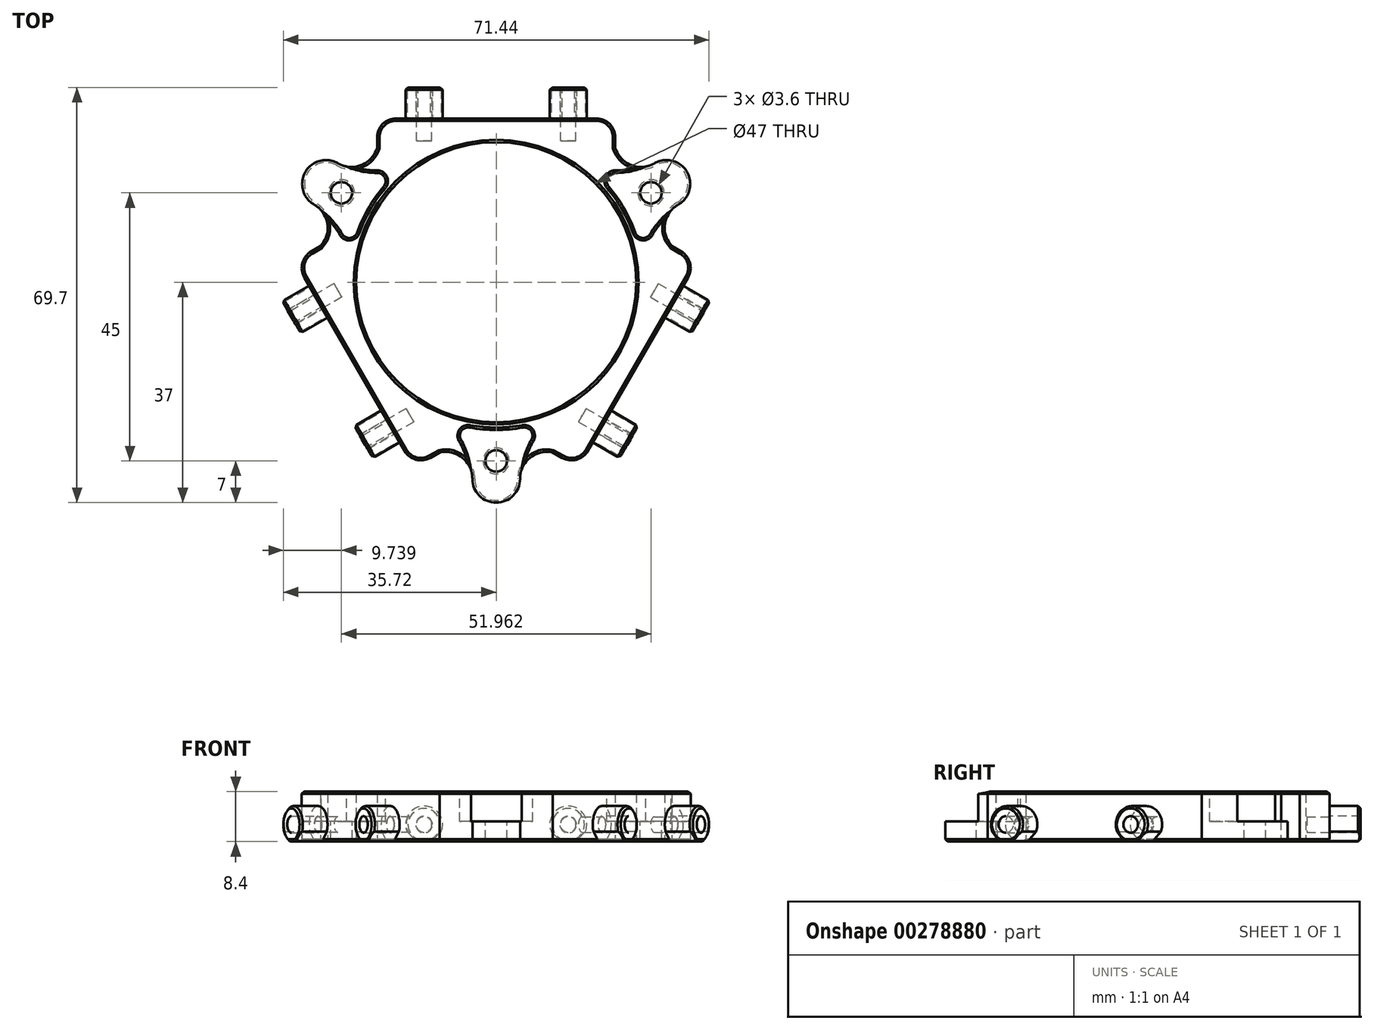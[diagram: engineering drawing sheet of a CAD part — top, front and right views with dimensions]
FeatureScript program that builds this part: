
annotation { "Feature Type Name" : "Feature", "Feature Type Description" : "" }
export const myFeature = defineFeature(function(context is Context, id is Id, definition is map)
    precondition{}
    {
        {
            var Q0;
            Q0=qCreatedBy(makeId("Top.planeOp"),FACE);
            var sketch = newSketch(context, id + "F0", { "sketchPlane" : qUnion([Q0])});
            skLineSegment(sketch, "E0", {"start": v(0, 27.5) * mm, "end": v(12, 27.5) * mm});
            skLineSegment(sketch, "E1", {"start": v(12, 27.5) * mm, "end": v(20, 27.5) * mm});
            skLineSegment(sketch, "E2", {"start": v(20, 27.5) * mm, "end": v(20, 22.5) * mm});
            skLineSegment(sketch, "E3.MirrorCS", {"start": v(0, 27.5) * mm, "end": v(-12, 27.5) * mm});
            skLineSegment(sketch, "E4.MirrorCS", {"start": v(-12, 27.5) * mm, "end": v(-20, 27.5) * mm});
            skLineSegment(sketch, "E5.MirrorCS", {"start": v(-20, 27.5) * mm, "end": v(-20, 22.5) * mm});
            skLineSegment(sketch, "E6.1.0", {"start": v(-13.82, -31.07) * mm, "end": v(-9.49, -28.57) * mm});
            skLineSegment(sketch, "E6.1.1", {"start": v(-33.82, 3.57) * mm, "end": v(-29.49, 6.07) * mm});
            skLineSegment(sketch, "E6.1.2", {"start": v(-23.82, -13.75) * mm, "end": v(-29.82, -3.36) * mm});
            skLineSegment(sketch, "E6.1.3", {"start": v(-29.82, -3.36) * mm, "end": v(-33.82, 3.57) * mm});
            skLineSegment(sketch, "E6.1.4", {"start": v(-23.82, -13.75) * mm, "end": v(-17.82, -24.14) * mm});
            skLineSegment(sketch, "E6.1.5", {"start": v(-17.82, -24.14) * mm, "end": v(-13.82, -31.07) * mm});
            skLineSegment(sketch, "E6.2.0", {"start": v(33.82, 3.57) * mm, "end": v(29.49, 6.07) * mm});
            skLineSegment(sketch, "E6.2.1", {"start": v(13.82, -31.07) * mm, "end": v(9.49, -28.57) * mm});
            skLineSegment(sketch, "E6.2.2", {"start": v(23.82, -13.75) * mm, "end": v(17.82, -24.14) * mm});
            skLineSegment(sketch, "E6.2.3", {"start": v(17.82, -24.14) * mm, "end": v(13.82, -31.07) * mm});
            skLineSegment(sketch, "E6.2.4", {"start": v(23.82, -13.75) * mm, "end": v(29.82, -3.36) * mm});
            skLineSegment(sketch, "E6.2.5", {"start": v(29.82, -3.36) * mm, "end": v(33.82, 3.57) * mm});
            skPoint(sketch, "E6.center", {"position": v(0, 0) * mm});
            skArc(sketch, "E7", {"start": v(-8.76, -23.41) * mm, "mid": v(0, -25) * mm, "end": v(8.76, -23.41) * mm});
            skCircle(sketch, "E8", {"center": v(0, -33) * mm, "radius": 4 * mm});
            skArc(sketch, "E9", {"start": v(8.76, -23.41) * mm, "mid": v(5.25, -27.65) * mm, "end": v(4, -33) * mm});
            skArc(sketch, "E10.MirrorCS", {"start": v(-8.76, -23.41) * mm, "mid": v(-5.25, -27.65) * mm, "end": v(-4, -33) * mm});
            skCircle(sketch, "E11", {"center": v(0, 0) * mm, "radius": 23.5 * mm});
            skArc(sketch, "E12", {"start": v(9.49, -28.57) * mm, "mid": v(5.67, -29.46) * mm, "end": v(4, -33) * mm});
            skArc(sketch, "E13.MirrorCS", {"start": v(-9.49, -28.57) * mm, "mid": v(-5.67, -29.46) * mm, "end": v(-4, -33) * mm});
            skCircle(sketch, "E14.1.0", {"center": v(28.58, 16.5) * mm, "radius": 4 * mm});
            skArc(sketch, "E14.1.1", {"start": v(20, 22.5) * mm, "mid": v(22.68, 19.64) * mm, "end": v(26.58, 19.96) * mm});
            skArc(sketch, "E14.1.2", {"start": v(29.49, 6.07) * mm, "mid": v(28.35, 9.82) * mm, "end": v(30.58, 13.04) * mm});
            skCircle(sketch, "E14.2.0", {"center": v(-28.58, 16.5) * mm, "radius": 4 * mm});
            skArc(sketch, "E14.2.1", {"start": v(-29.49, 6.07) * mm, "mid": v(-28.35, 9.82) * mm, "end": v(-30.58, 13.04) * mm});
            skArc(sketch, "E14.2.2", {"start": v(-20, 22.5) * mm, "mid": v(-22.68, 19.64) * mm, "end": v(-26.58, 19.96) * mm});
            skSolve(sketch);
        }
        {
            var Q0;
            Q0=qSketchRegion(id+"F0",true);
            extrude(context, id + "F1", {"entities" : qUnion([Q0]), "depth" : 8.4 * mm, "offsetDistance" : 25 * mm});
        }
        {
            var Q0;
            Q0=makeQuery(id+"F1.opExtrude","SWEPT_FACE",FACE,{"disambiguationData":[OSD([sQuery(id+"F0.wireOp",EDGE,"E0"),sQuery(id+"F0.wireOp",EDGE,"E1"),sQuery(id+"F0.wireOp",EDGE,"E3.MirrorCS"),sQuery(id+"F0.wireOp",EDGE,"E4.MirrorCS")])]});
            var sketch = newSketch(context, id + "F2", { "sketchPlane" : qUnion([Q0])});
            skCircle(sketch, "E15.cCircle", {"center": v(-12.1, 2.86) * mm, "radius": 2.86 * mm, "construction": true});
            skLineSegment(sketch, "E15.0", {"start": v(-13.29, 5.73) * mm, "end": v(-10.91, 5.73) * mm});
            skLineSegment(sketch, "E15.1", {"start": v(-10.91, 5.73) * mm, "end": v(-9.24, 4.05) * mm});
            skLineSegment(sketch, "E15.2", {"start": v(-9.24, 4.05) * mm, "end": v(-9.24, 1.68) * mm});
            skLineSegment(sketch, "E15.3", {"start": v(-9.24, 1.68) * mm, "end": v(-10.91, 0) * mm});
            skLineSegment(sketch, "E15.4", {"start": v(-10.91, 0) * mm, "end": v(-13.29, 0) * mm});
            skLineSegment(sketch, "E15.5", {"start": v(-13.29, 0) * mm, "end": v(-14.96, 1.68) * mm});
            skLineSegment(sketch, "E15.6", {"start": v(-14.96, 1.68) * mm, "end": v(-14.96, 4.05) * mm});
            skLineSegment(sketch, "E15.7", {"start": v(-14.96, 4.05) * mm, "end": v(-13.29, 5.73) * mm});
            skPoint(sketch, "E15.0.midPoint", {"position": v(-12.1, 5.73) * mm});
            skArc(sketch, "E16", {"start": v(-9.24, 1.68) * mm, "mid": v(-12.1, 5.96) * mm, "end": v(-14.96, 1.68) * mm});
            skLineSegment(sketch, "E17.MirrorCS", {"start": v(10.91, 5.73) * mm, "end": v(9.24, 4.05) * mm});
            skLineSegment(sketch, "E18.MirrorCS", {"start": v(9.24, 4.05) * mm, "end": v(9.24, 1.68) * mm});
            skLineSegment(sketch, "E19.MirrorCS", {"start": v(14.96, 1.68) * mm, "end": v(14.96, 4.05) * mm});
            skLineSegment(sketch, "E20.MirrorCS", {"start": v(9.24, 1.68) * mm, "end": v(10.91, 0) * mm});
            skLineSegment(sketch, "E21.MirrorCS", {"start": v(14.96, 4.05) * mm, "end": v(13.29, 5.73) * mm});
            skLineSegment(sketch, "E22.MirrorCS", {"start": v(13.29, 5.73) * mm, "end": v(10.91, 5.73) * mm});
            skLineSegment(sketch, "E23.MirrorCS", {"start": v(10.91, 0) * mm, "end": v(13.29, 0) * mm});
            skLineSegment(sketch, "E24.MirrorCS", {"start": v(13.29, 0) * mm, "end": v(14.96, 1.68) * mm});
            skArc(sketch, "E25.MirrorCS", {"start": v(9.24, 1.68) * mm, "mid": v(12.1, 5.96) * mm, "end": v(14.96, 1.68) * mm});
            skPoint(sketch, "E26.MirrorP", {"position": v(12.1, 5.73) * mm});
            skCircle(sketch, "E27.MirrorC", {"center": v(12.1, 2.86) * mm, "radius": 2.86 * mm, "construction": true});
            skCircle(sketch, "E28", {"center": v(-12.1, 2.86) * mm, "radius": 1.4 * mm});
            skCircle(sketch, "E29.MirrorC", {"center": v(12.1, 2.86) * mm, "radius": 1.4 * mm});
            skSolve(sketch);
        }
        {
            var Q0;
            Q0=qSketchRegion(id+"F2",true);
            extrude(context, id + "F3", {"entities" : qUnion([Q0]), "depth" : 5.2 * mm, "offsetDistance" : 25 * mm});
        }
        {
            var Q0;
            Q0=makeQuery(id+"F3.opExtrude","SWEPT_BODY",BODY,{"disambiguationData":[OSD([sQuery(id+"F2.wireOp",EDGE,"E15.0"),sQuery(id+"F2.wireOp",EDGE,"E15.1"),sQuery(id+"F2.wireOp",EDGE,"E15.2"),sQuery(id+"F2.wireOp",EDGE,"E15.3"),sQuery(id+"F2.wireOp",EDGE,"E15.4"),sQuery(id+"F2.wireOp",EDGE,"E15.5"),sQuery(id+"F2.wireOp",EDGE,"E15.6"),sQuery(id+"F2.wireOp",EDGE,"E15.7")])]});
            var Q1;
            Q1=makeQuery(id+"F3.opExtrude","SWEPT_BODY",BODY,{"disambiguationData":[OSD([sQuery(id+"F2.wireOp",EDGE,"E20.MirrorCS"),sQuery(id+"F2.wireOp",EDGE,"E23.MirrorCS"),sQuery(id+"F2.wireOp",EDGE,"E24.MirrorCS"),sQuery(id+"F2.wireOp",EDGE,"E25.MirrorCS")])]});
            var Q2;
            Q2=makeQuery(id+"F1.opExtrude","CAP_EDGE",EDGE,{"disambiguationData":[OSD([sQuery(id+"F0.wireOp",EDGE,"E11")])],"isStart":false});
            circularPattern(context, id + "F4", {"operationType" : NewBodyOperationType.ADD, "entities" : qUnion([Q0, Q1]), "axis" : qUnion([Q2]), "angle" : 360 * degree, "instanceCount" : 3, "equalSpace" : true});
        }
        {
            var Q0;
            Q0=makeQuery(id+"F3.opExtrude","CAP_FACE",FACE,{"disambiguationData":[OSD([sQuery(id+"F2.wireOp",EDGE,"E15.3"),sQuery(id+"F2.wireOp",EDGE,"E15.4"),sQuery(id+"F2.wireOp",EDGE,"E15.5"),sQuery(id+"F2.wireOp",EDGE,"E16")])],"isStart":false});
            var sketch = newSketch(context, id + "F5", { "sketchPlane" : qUnion([Q0])});
            skCircle(sketch, "E30", {"center": v(-12.1, 2.86) * mm, "radius": 1.3 * mm});
            skCircle(sketch, "E31.MirrorC", {"center": v(12.1, 2.86) * mm, "radius": 1.3 * mm});
            skSolve(sketch);
        }
        {
            var Q0;
            Q0=qSketchRegion(id+"F5",true);
            extrude(context, id + "F6", {"entities" : qUnion([Q0]), "oppositeDirection" : true, "depth" : 9 * mm, "offsetDistance" : 25 * mm});
        }
        {
            var Q0;
            Q0=makeQuery(id+"F6.opExtrude","SWEPT_BODY",BODY,{"disambiguationData":[OSD([sQuery(id+"F5.wireOp",EDGE,"E31.MirrorC")])]});
            var Q1;
            Q1=makeQuery(id+"F6.opExtrude","SWEPT_BODY",BODY,{"disambiguationData":[OSD([sQuery(id+"F5.wireOp",EDGE,"E30")])]});
            var Q2;
            Q2=makeQuery(id+"F1.opExtrude","CAP_EDGE",EDGE,{"disambiguationData":[OSD([sQuery(id+"F0.wireOp",EDGE,"E11")])],"isStart":false});
            circularPattern(context, id + "F7", {"operationType" : NewBodyOperationType.REMOVE, "entities" : qUnion([Q0, Q1]), "axis" : qUnion([Q2]), "angle" : 360 * degree, "instanceCount" : 3, "equalSpace" : true});
        }
        {
            var Q0;
            Q0=makeQuery(id+"F1.opExtrude","CAP_FACE",FACE,{"disambiguationData":[OSD([sQuery(id+"F0.wireOp",EDGE,"4484d7a0-2c50-4ab7-845c-1fad09a73396"),sQuery(id+"F0.wireOp",EDGE,"vunMmcyM-OmEz-jSXp-RP42-2TM2nteFIjq3"),sQuery(id+"F0.wireOp",EDGE,"kAdxAM4n-0fVD-Q49A-3DVH-t19awp9mxCRN"),sQuery(id+"F0.wireOp",EDGE,"1fc718da-6f13-47b3-b5a0-f714b977743f0.MirrorCS"),sQuery(id+"F0.wireOp",EDGE,"0c3f0dc6-742d-4421-8c8e-992fc040e4260.MirrorCS"),sQuery(id+"F0.wireOp",EDGE,"NR2aZ9zS-O8kZ-dOxt-Ha0G-w07LVY2dGel9"),sQuery(id+"F0.wireOp",EDGE,"E0"),sQuery(id+"F0.wireOp",EDGE,"E1"),sQuery(id+"F0.wireOp",EDGE,"E2"),sQuery(id+"F0.wireOp",EDGE,"E3.MirrorCS"),sQuery(id+"F0.wireOp",EDGE,"E4.MirrorCS"),sQuery(id+"F0.wireOp",EDGE,"E5.MirrorCS"),sQuery(id+"F0.wireOp",EDGE,"b799197c-b9e2-4d90-802a-dec7aafa3731.1.0"),sQuery(id+"F0.wireOp",EDGE,"b799197c-b9e2-4d90-802a-dec7aafa3731.1.1"),sQuery(id+"F0.wireOp",EDGE,"b799197c-b9e2-4d90-802a-dec7aafa3731.1.2"),sQuery(id+"F0.wireOp",EDGE,"b799197c-b9e2-4d90-802a-dec7aafa3731.1.3"),sQuery(id+"F0.wireOp",EDGE,"b799197c-b9e2-4d90-802a-dec7aafa3731.1.4"),sQuery(id+"F0.wireOp",EDGE,"b799197c-b9e2-4d90-802a-dec7aafa3731.1.5"),sQuery(id+"F0.wireOp",EDGE,"b799197c-b9e2-4d90-802a-dec7aafa3731.2.0"),sQuery(id+"F0.wireOp",EDGE,"b799197c-b9e2-4d90-802a-dec7aafa3731.2.1"),sQuery(id+"F0.wireOp",EDGE,"b799197c-b9e2-4d90-802a-dec7aafa3731.2.2"),sQuery(id+"F0.wireOp",EDGE,"b799197c-b9e2-4d90-802a-dec7aafa3731.2.3"),sQuery(id+"F0.wireOp",EDGE,"b799197c-b9e2-4d90-802a-dec7aafa3731.2.4"),sQuery(id+"F0.wireOp",EDGE,"b799197c-b9e2-4d90-802a-dec7aafa3731.2.5"),sQuery(id+"F0.wireOp",EDGE,"Wg4TRRuH-37hh-Xavb-2tcF-YoE0x18wPgdB"),sQuery(id+"F0.wireOp",EDGE,"0f9c7b85-d36a-485b-916f-4e3243d4aea60.MirrorCS"),sQuery(id+"F0.wireOp",EDGE,"b2d11125-5d0d-4662-a4de-013f4188032f.1.0"),sQuery(id+"F0.wireOp",EDGE,"b2d11125-5d0d-4662-a4de-013f4188032f.1.2"),sQuery(id+"F0.wireOp",EDGE,"b2d11125-5d0d-4662-a4de-013f4188032f.1.3"),sQuery(id+"F0.wireOp",EDGE,"b2d11125-5d0d-4662-a4de-013f4188032f.1.7"),sQuery(id+"F0.wireOp",EDGE,"b2d11125-5d0d-4662-a4de-013f4188032f.1.8"),sQuery(id+"F0.wireOp",EDGE,"b2d11125-5d0d-4662-a4de-013f4188032f.1.9"),sQuery(id+"F0.wireOp",EDGE,"b2d11125-5d0d-4662-a4de-013f4188032f.1.10"),sQuery(id+"F0.wireOp",EDGE,"b2d11125-5d0d-4662-a4de-013f4188032f.2.0"),sQuery(id+"F0.wireOp",EDGE,"b2d11125-5d0d-4662-a4de-013f4188032f.2.2"),sQuery(id+"F0.wireOp",EDGE,"b2d11125-5d0d-4662-a4de-013f4188032f.2.3"),sQuery(id+"F0.wireOp",EDGE,"b2d11125-5d0d-4662-a4de-013f4188032f.2.7"),sQuery(id+"F0.wireOp",EDGE,"b2d11125-5d0d-4662-a4de-013f4188032f.2.8"),sQuery(id+"F0.wireOp",EDGE,"b2d11125-5d0d-4662-a4de-013f4188032f.2.9"),sQuery(id+"F0.wireOp",EDGE,"b2d11125-5d0d-4662-a4de-013f4188032f.2.10")])],"isStart":false});
            var sketch = newSketch(context, id + "F8", { "sketchPlane" : qUnion([Q0])});
            skArc(sketch, "E32", {"start": v(-8.86, -23.16) * mm, "mid": v(0, -24.8) * mm, "end": v(8.86, -23.16) * mm});
            skCircle(sketch, "E33", {"center": v(0, -33) * mm, "radius": 4.2 * mm});
            skArc(sketch, "E34", {"start": v(8.86, -23.16) * mm, "mid": v(5.35, -27.52) * mm, "end": v(4.2, -33) * mm});
            skArc(sketch, "E35.MirrorCS", {"start": v(-8.86, -23.16) * mm, "mid": v(-5.35, -27.52) * mm, "end": v(-4.2, -33) * mm});
            skArc(sketch, "E36.1.0", {"start": v(24.5, 3.9) * mm, "mid": v(26.51, 9.13) * mm, "end": v(30.68, 12.86) * mm});
            skArc(sketch, "E36.1.1", {"start": v(24.5, 3.9) * mm, "mid": v(21.48, 12.4) * mm, "end": v(15.63, 19.26) * mm});
            skArc(sketch, "E36.1.2", {"start": v(15.63, 19.26) * mm, "mid": v(21.16, 18.4) * mm, "end": v(26.48, 20.14) * mm});
            skCircle(sketch, "E36.1.3", {"center": v(28.58, 16.5) * mm, "radius": 4.2 * mm});
            skArc(sketch, "E36.2.0", {"start": v(-15.63, 19.26) * mm, "mid": v(-21.16, 18.4) * mm, "end": v(-26.48, 20.14) * mm});
            skArc(sketch, "E36.2.1", {"start": v(-15.63, 19.26) * mm, "mid": v(-21.48, 12.4) * mm, "end": v(-24.5, 3.9) * mm});
            skArc(sketch, "E36.2.2", {"start": v(-24.5, 3.9) * mm, "mid": v(-26.51, 9.13) * mm, "end": v(-30.68, 12.86) * mm});
            skCircle(sketch, "E36.2.3", {"center": v(-28.58, 16.5) * mm, "radius": 4.2 * mm});
            skSolve(sketch);
        }
        {
            var Q0;
            Q0=qSketchRegion(id+"F8",true);
            extrude(context, id + "F9", {"entities" : qUnion([Q0]), "oppositeDirection" : true, "depth" : 5 * mm, "offsetDistance" : 25 * mm});
        }
        {
            var Q0;
            Q0=makeQuery(id+"F9.opExtrude","SWEPT_EDGE",EDGE,{"disambiguationData":[OSD([sQuery(id+"F8.wireOp",EDGE,"E32"),sQuery(id+"F8.wireOp",EDGE,"E34")])]});
            var Q1;
            Q1=makeQuery(id+"F9.opExtrude","SWEPT_EDGE",EDGE,{"disambiguationData":[OSD([sQuery(id+"F8.wireOp",EDGE,"E32"),sQuery(id+"F8.wireOp",EDGE,"E35.MirrorCS")])]});
            var Q2;
            Q2=makeQuery(id+"F9.opExtrude","SWEPT_EDGE",EDGE,{"disambiguationData":[OSD([sQuery(id+"F8.wireOp",EDGE,"E36.1.0"),sQuery(id+"F8.wireOp",EDGE,"E36.1.1")])]});
            var Q3;
            Q3=makeQuery(id+"F9.opExtrude","SWEPT_EDGE",EDGE,{"disambiguationData":[OSD([sQuery(id+"F8.wireOp",EDGE,"E36.1.1"),sQuery(id+"F8.wireOp",EDGE,"E36.1.2")])]});
            var Q4;
            Q4=makeQuery(id+"F9.opExtrude","SWEPT_EDGE",EDGE,{"disambiguationData":[OSD([sQuery(id+"F8.wireOp",EDGE,"E36.2.0"),sQuery(id+"F8.wireOp",EDGE,"E36.2.1")])]});
            var Q5;
            Q5=makeQuery(id+"F9.opExtrude","SWEPT_EDGE",EDGE,{"disambiguationData":[OSD([sQuery(id+"F8.wireOp",EDGE,"E36.2.1"),sQuery(id+"F8.wireOp",EDGE,"E36.2.2")])]});
            fillet(context, id + "F10", {"entities" : qUnion([Q0, Q1, Q2, Q3, Q4, Q5]), "radius" : 1.4 * mm, "tangentPropagation" : true, "allowEdgeOverflow" : false});
        }
        {
            var Q0;
            Q0=makeQuery(id+"F9.opExtrude","SWEPT_BODY",BODY,{"disambiguationData":[OSD([sQuery(id+"F8.wireOp",EDGE,"E32"),sQuery(id+"F8.wireOp",EDGE,"E33"),sQuery(id+"F8.wireOp",EDGE,"E34"),sQuery(id+"F8.wireOp",EDGE,"E35.MirrorCS")])]});
            var Q1;
            Q1=makeQuery(id+"F9.opExtrude","SWEPT_BODY",BODY,{"disambiguationData":[OSD([sQuery(id+"F8.wireOp",EDGE,"E36.1.0"),sQuery(id+"F8.wireOp",EDGE,"E36.1.1"),sQuery(id+"F8.wireOp",EDGE,"E36.1.2"),sQuery(id+"F8.wireOp",EDGE,"E36.1.3")])]});
            var Q2;
            Q2=makeQuery(id+"F9.opExtrude","SWEPT_BODY",BODY,{"disambiguationData":[OSD([sQuery(id+"F8.wireOp",EDGE,"E36.2.0"),sQuery(id+"F8.wireOp",EDGE,"E36.2.1"),sQuery(id+"F8.wireOp",EDGE,"E36.2.2"),sQuery(id+"F8.wireOp",EDGE,"E36.2.3")])]});
            var Q3;
            Q3=makeQuery(id+"F1.opExtrude","SWEPT_BODY",BODY,{"disambiguationData":[OSD([sQuery(id+"F0.wireOp",EDGE,"E0"),sQuery(id+"F0.wireOp",EDGE,"E1"),sQuery(id+"F0.wireOp",EDGE,"E2"),sQuery(id+"F0.wireOp",EDGE,"E3.MirrorCS"),sQuery(id+"F0.wireOp",EDGE,"E4.MirrorCS"),sQuery(id+"F0.wireOp",EDGE,"E5.MirrorCS"),sQuery(id+"F0.wireOp",EDGE,"E6.1.0"),sQuery(id+"F0.wireOp",EDGE,"E6.1.1"),sQuery(id+"F0.wireOp",EDGE,"E6.1.2"),sQuery(id+"F0.wireOp",EDGE,"E6.1.3"),sQuery(id+"F0.wireOp",EDGE,"E6.1.4"),sQuery(id+"F0.wireOp",EDGE,"E6.1.5"),sQuery(id+"F0.wireOp",EDGE,"E6.2.0"),sQuery(id+"F0.wireOp",EDGE,"E6.2.1"),sQuery(id+"F0.wireOp",EDGE,"E6.2.2"),sQuery(id+"F0.wireOp",EDGE,"E6.2.3"),sQuery(id+"F0.wireOp",EDGE,"E6.2.4"),sQuery(id+"F0.wireOp",EDGE,"E6.2.5"),sQuery(id+"F0.wireOp",EDGE,"E8"),sQuery(id+"F0.wireOp",EDGE,"E9"),sQuery(id+"F0.wireOp",EDGE,"E10.MirrorCS"),sQuery(id+"F0.wireOp",EDGE,"E11"),sQuery(id+"F0.wireOp",EDGE,"E12"),sQuery(id+"F0.wireOp",EDGE,"E13.MirrorCS"),sQuery(id+"F0.wireOp",EDGE,"E14.1.0"),sQuery(id+"F0.wireOp",EDGE,"E14.1.1"),sQuery(id+"F0.wireOp",EDGE,"E14.1.2"),sQuery(id+"F0.wireOp",EDGE,"E14.2.0"),sQuery(id+"F0.wireOp",EDGE,"E14.2.1"),sQuery(id+"F0.wireOp",EDGE,"E14.2.2")])]});
            booleanBodies(context, id + "F11", {"operationType" : BooleanOperationType.SUBTRACTION, "tools" : qUnion([Q0, Q1, Q2]), "targets" : qUnion([Q3])});
        }
        {
            var Q0;
            Q0=makeQuery(id+"F1.opExtrude","CAP_FACE",FACE,{"disambiguationData":[OSD([sQuery(id+"F0.wireOp",EDGE,"E0"),sQuery(id+"F0.wireOp",EDGE,"E1"),sQuery(id+"F0.wireOp",EDGE,"E2"),sQuery(id+"F0.wireOp",EDGE,"E3.MirrorCS"),sQuery(id+"F0.wireOp",EDGE,"E4.MirrorCS"),sQuery(id+"F0.wireOp",EDGE,"E5.MirrorCS"),sQuery(id+"F0.wireOp",EDGE,"E6.1.0"),sQuery(id+"F0.wireOp",EDGE,"E6.1.1"),sQuery(id+"F0.wireOp",EDGE,"E6.1.2"),sQuery(id+"F0.wireOp",EDGE,"E6.1.3"),sQuery(id+"F0.wireOp",EDGE,"E6.1.4"),sQuery(id+"F0.wireOp",EDGE,"E6.1.5"),sQuery(id+"F0.wireOp",EDGE,"E6.2.0"),sQuery(id+"F0.wireOp",EDGE,"E6.2.1"),sQuery(id+"F0.wireOp",EDGE,"E6.2.2"),sQuery(id+"F0.wireOp",EDGE,"E6.2.3"),sQuery(id+"F0.wireOp",EDGE,"E6.2.4"),sQuery(id+"F0.wireOp",EDGE,"E6.2.5"),sQuery(id+"F0.wireOp",EDGE,"E8"),sQuery(id+"F0.wireOp",EDGE,"E9"),sQuery(id+"F0.wireOp",EDGE,"E10.MirrorCS"),sQuery(id+"F0.wireOp",EDGE,"E11"),sQuery(id+"F0.wireOp",EDGE,"E12"),sQuery(id+"F0.wireOp",EDGE,"E13.MirrorCS"),sQuery(id+"F0.wireOp",EDGE,"E14.1.0"),sQuery(id+"F0.wireOp",EDGE,"E14.1.1"),sQuery(id+"F0.wireOp",EDGE,"E14.1.2"),sQuery(id+"F0.wireOp",EDGE,"E14.2.0"),sQuery(id+"F0.wireOp",EDGE,"E14.2.1"),sQuery(id+"F0.wireOp",EDGE,"E14.2.2")])],"isStart":false});
            var sketch = newSketch(context, id + "F12", { "sketchPlane" : qUnion([Q0])});
            skCircle(sketch, "E37", {"center": v(0, -30) * mm, "radius": 1.8 * mm});
            skCircle(sketch, "E38.1.0", {"center": v(25.98, 15) * mm, "radius": 1.8 * mm});
            skCircle(sketch, "E38.2.0", {"center": v(-25.98, 15) * mm, "radius": 1.8 * mm});
            skPoint(sketch, "E38.center", {"position": v(0, 0) * mm});
            skSolve(sketch);
        }
        {
            var Q0;
            Q0 = qSketchRegion(id + "F12", true);
            var Q1;
            {var subQ0=makeQuery(id+"F3.opExtrude","SWEPT_FACE",FACE,{"disambiguationData":[OSD([sQuery(id+"F2.wireOp",EDGE,"E23.MirrorCS")])]});var subQ1=makeQuery(id+"F3.opExtrude","SWEPT_FACE",FACE,{"disambiguationData":[OSD([sQuery(id+"F2.wireOp",EDGE,"E15.4")])]});Q1=makeQuery(id+"F4.boolean.opBoolean","MERGE",FACE,{"derivedFrom":[makeQuery(id+"F1.opExtrude","CAP_FACE",FACE,{"disambiguationData":[OSD([sQuery(id+"F0.wireOp",EDGE,"E0"),sQuery(id+"F0.wireOp",EDGE,"E1"),sQuery(id+"F0.wireOp",EDGE,"E2"),sQuery(id+"F0.wireOp",EDGE,"E3.MirrorCS"),sQuery(id+"F0.wireOp",EDGE,"E4.MirrorCS"),sQuery(id+"F0.wireOp",EDGE,"E5.MirrorCS"),sQuery(id+"F0.wireOp",EDGE,"E6.1.0"),sQuery(id+"F0.wireOp",EDGE,"E6.1.1"),sQuery(id+"F0.wireOp",EDGE,"E6.1.2"),sQuery(id+"F0.wireOp",EDGE,"E6.1.3"),sQuery(id+"F0.wireOp",EDGE,"E6.1.4"),sQuery(id+"F0.wireOp",EDGE,"E6.1.5"),sQuery(id+"F0.wireOp",EDGE,"E6.2.0"),sQuery(id+"F0.wireOp",EDGE,"E6.2.1"),sQuery(id+"F0.wireOp",EDGE,"E6.2.2"),sQuery(id+"F0.wireOp",EDGE,"E6.2.3"),sQuery(id+"F0.wireOp",EDGE,"E6.2.4"),sQuery(id+"F0.wireOp",EDGE,"E6.2.5"),sQuery(id+"F0.wireOp",EDGE,"E8"),sQuery(id+"F0.wireOp",EDGE,"E9"),sQuery(id+"F0.wireOp",EDGE,"E10.MirrorCS"),sQuery(id+"F0.wireOp",EDGE,"E11"),sQuery(id+"F0.wireOp",EDGE,"E12"),sQuery(id+"F0.wireOp",EDGE,"E13.MirrorCS"),sQuery(id+"F0.wireOp",EDGE,"E14.1.0"),sQuery(id+"F0.wireOp",EDGE,"E14.1.1"),sQuery(id+"F0.wireOp",EDGE,"E14.1.2"),sQuery(id+"F0.wireOp",EDGE,"E14.2.0"),sQuery(id+"F0.wireOp",EDGE,"E14.2.1"),sQuery(id+"F0.wireOp",EDGE,"E14.2.2")])],"isStart":true}),subQ1,subQ0,makeQuery(id+"F4.opPattern","COPY",FACE,{"derivedFrom":subQ1,"instanceName":"1"}),makeQuery(id+"F4.opPattern","COPY",FACE,{"derivedFrom":subQ0,"instanceName":"1"}),makeQuery(id+"F4.opPattern","COPY",FACE,{"derivedFrom":subQ1,"instanceName":"2"}),makeQuery(id+"F4.opPattern","COPY",FACE,{"derivedFrom":subQ0,"instanceName":"2"})]});}
            extrude(context, id + "F13", {"entities" : qUnion([Q0]), "operationType" : NewBodyOperationType.REMOVE, "endBound" : BoundingType.UP_TO_SURFACE, "oppositeDirection" : true, "depth" : 25 * mm, "endBoundEntityFace" : qUnion([Q1]), "offsetDistance" : 25 * mm});
        }
        {
            var Q0;
            Q0=makeQuery(id+"F1.opExtrude","SWEPT_EDGE",EDGE,{"disambiguationData":[OSD([sQuery(id+"F0.wireOp",EDGE,"E1"),sQuery(id+"F0.wireOp",EDGE,"E2")])]});
            var Q1;
            Q1=makeQuery(id+"F1.opExtrude","SWEPT_EDGE",EDGE,{"disambiguationData":[OSD([sQuery(id+"F0.wireOp",EDGE,"E4.MirrorCS"),sQuery(id+"F0.wireOp",EDGE,"E5.MirrorCS")])]});
            var Q2;
            Q2=makeQuery(id+"F1.opExtrude","SWEPT_EDGE",EDGE,{"disambiguationData":[OSD([sQuery(id+"F0.wireOp",EDGE,"E6.2.0"),sQuery(id+"F0.wireOp",EDGE,"E6.2.5")])]});
            var Q3;
            Q3=makeQuery(id+"F1.opExtrude","SWEPT_EDGE",EDGE,{"disambiguationData":[OSD([sQuery(id+"F0.wireOp",EDGE,"E6.2.1"),sQuery(id+"F0.wireOp",EDGE,"E6.2.3")])]});
            var Q4;
            Q4=makeQuery(id+"F1.opExtrude","SWEPT_EDGE",EDGE,{"disambiguationData":[OSD([sQuery(id+"F0.wireOp",EDGE,"E6.1.0"),sQuery(id+"F0.wireOp",EDGE,"E6.1.5")])]});
            var Q5;
            Q5=makeQuery(id+"F1.opExtrude","SWEPT_EDGE",EDGE,{"disambiguationData":[OSD([sQuery(id+"F0.wireOp",EDGE,"E6.1.1"),sQuery(id+"F0.wireOp",EDGE,"E6.1.3")])]});
            fillet(context, id + "F14", {"entities" : qUnion([Q0, Q1, Q2, Q3, Q4, Q5]), "radius" : 3.2 * mm, "tangentPropagation" : true, "allowEdgeOverflow" : false});
        }
        {
            var Q0;
            {var subQ0=makeQuery(id+"F3.opExtrude","SWEPT_FACE",FACE,{"disambiguationData":[OSD([sQuery(id+"F2.wireOp",EDGE,"E23.MirrorCS")])]});var subQ1=makeQuery(id+"F3.opExtrude","SWEPT_FACE",FACE,{"disambiguationData":[OSD([sQuery(id+"F2.wireOp",EDGE,"E15.4")])]});Q0=makeQuery(id+"F4.boolean.opBoolean","MERGE",FACE,{"derivedFrom":[makeQuery(id+"F1.opExtrude","CAP_FACE",FACE,{"disambiguationData":[OSD([sQuery(id+"F0.wireOp",EDGE,"SqP7JoLz-BD9A-RXmz-Zu1V-RbqKSFD4Gl63"),sQuery(id+"F0.wireOp",EDGE,"Ud9Chbpr-zYe2-2spb-ifSY-rzAQWNdjOQxf"),sQuery(id+"F0.wireOp",EDGE,"bF6wv58Z-VzMq-CWjE-Sgwb-4WXWosELiao8"),sQuery(id+"F0.wireOp",EDGE,"cTkBJLnt-Smek-8MJw-4hbo-giizK2urv45t"),sQuery(id+"F0.wireOp",EDGE,"ae239fa6-1cef-4aa7-9151-0311c269b8940.MirrorCS"),sQuery(id+"F0.wireOp",EDGE,"ae239fa6-1cef-4aa7-9151-0311c269b8941.MirrorCS"),sQuery(id+"F0.wireOp",EDGE,"ae239fa6-1cef-4aa7-9151-0311c269b8943.MirrorCS"),sQuery(id+"F0.wireOp",EDGE,"ae239fa6-1cef-4aa7-9151-0311c269b8946.MirrorCS"),sQuery(id+"F0.wireOp",EDGE,"02da523c-332d-451a-b30c-e25d5381daab.1.0"),sQuery(id+"F0.wireOp",EDGE,"02da523c-332d-451a-b30c-e25d5381daab.1.1"),sQuery(id+"F0.wireOp",EDGE,"02da523c-332d-451a-b30c-e25d5381daab.1.2"),sQuery(id+"F0.wireOp",EDGE,"02da523c-332d-451a-b30c-e25d5381daab.1.5"),sQuery(id+"F0.wireOp",EDGE,"02da523c-332d-451a-b30c-e25d5381daab.1.6"),sQuery(id+"F0.wireOp",EDGE,"02da523c-332d-451a-b30c-e25d5381daab.1.8"),sQuery(id+"F0.wireOp",EDGE,"02da523c-332d-451a-b30c-e25d5381daab.1.9"),sQuery(id+"F0.wireOp",EDGE,"02da523c-332d-451a-b30c-e25d5381daab.1.15"),sQuery(id+"F0.wireOp",EDGE,"02da523c-332d-451a-b30c-e25d5381daab.1.16"),sQuery(id+"F0.wireOp",EDGE,"02da523c-332d-451a-b30c-e25d5381daab.2.0"),sQuery(id+"F0.wireOp",EDGE,"02da523c-332d-451a-b30c-e25d5381daab.2.1"),sQuery(id+"F0.wireOp",EDGE,"02da523c-332d-451a-b30c-e25d5381daab.2.2"),sQuery(id+"F0.wireOp",EDGE,"02da523c-332d-451a-b30c-e25d5381daab.2.5"),sQuery(id+"F0.wireOp",EDGE,"02da523c-332d-451a-b30c-e25d5381daab.2.6"),sQuery(id+"F0.wireOp",EDGE,"02da523c-332d-451a-b30c-e25d5381daab.2.8"),sQuery(id+"F0.wireOp",EDGE,"02da523c-332d-451a-b30c-e25d5381daab.2.9"),sQuery(id+"F0.wireOp",EDGE,"02da523c-332d-451a-b30c-e25d5381daab.2.11"),sQuery(id+"F0.wireOp",EDGE,"02da523c-332d-451a-b30c-e25d5381daab.2.15"),sQuery(id+"F0.wireOp",EDGE,"02da523c-332d-451a-b30c-e25d5381daab.2.16"),sQuery(id+"F0.wireOp",EDGE,"tuegAIGZ-9Pk6-ZTlW-QU7Y-IGKE2iZstJ9h"),sQuery(id+"F0.wireOp",EDGE,"fd02a02f-7cdf-416c-a631-e7393bf9c9300.MirrorC"),sQuery(id+"F0.wireOp",EDGE,"b5a6a487-fcb2-4526-9c33-14607ead2c7a.1.0"),sQuery(id+"F0.wireOp",EDGE,"b5a6a487-fcb2-4526-9c33-14607ead2c7a.1.1"),sQuery(id+"F0.wireOp",EDGE,"b5a6a487-fcb2-4526-9c33-14607ead2c7a.2.0"),sQuery(id+"F0.wireOp",EDGE,"b5a6a487-fcb2-4526-9c33-14607ead2c7a.2.1")])],"isStart":true}),subQ1,subQ0,makeQuery(id+"F4.opPattern","COPY",FACE,{"derivedFrom":subQ1,"instanceName":"1"}),makeQuery(id+"F4.opPattern","COPY",FACE,{"derivedFrom":subQ0,"instanceName":"1"}),makeQuery(id+"F4.opPattern","COPY",FACE,{"derivedFrom":subQ1,"instanceName":"2"}),makeQuery(id+"F4.opPattern","COPY",FACE,{"derivedFrom":subQ0,"instanceName":"2"})]});}
            var Q1;
            Q1=makeQuery(id+"F3.opExtrude","CAP_EDGE",EDGE,{"disambiguationData":[OSD([sQuery(id+"F2.wireOp",EDGE,"E25.MirrorCS")])],"isStart":false});
            var Q2;
            Q2=makeQuery(id+"F3.opExtrude","CAP_EDGE",EDGE,{"disambiguationData":[OSD([sQuery(id+"F2.wireOp",EDGE,"E16")])],"isStart":false});
            var Q3;
            Q3=makeQuery(id+"F4.opPattern","COPY",EDGE,{"derivedFrom":makeQuery(id+"F3.opExtrude","CAP_EDGE",EDGE,{"disambiguationData":[OSD([sQuery(id+"F2.wireOp",EDGE,"E25.MirrorCS")])],"isStart":false}),"instanceName":"2"});
            var Q4;
            Q4=makeQuery(id+"F4.opPattern","COPY",EDGE,{"derivedFrom":makeQuery(id+"F3.opExtrude","CAP_EDGE",EDGE,{"disambiguationData":[OSD([sQuery(id+"F2.wireOp",EDGE,"E16")])],"isStart":false}),"instanceName":"2"});
            var Q5;
            Q5=makeQuery(id+"F4.opPattern","COPY",EDGE,{"derivedFrom":makeQuery(id+"F3.opExtrude","CAP_EDGE",EDGE,{"disambiguationData":[OSD([sQuery(id+"F2.wireOp",EDGE,"E25.MirrorCS")])],"isStart":false}),"instanceName":"1"});
            var Q6;
            Q6=makeQuery(id+"F4.opPattern","COPY",EDGE,{"derivedFrom":makeQuery(id+"F3.opExtrude","CAP_EDGE",EDGE,{"disambiguationData":[OSD([sQuery(id+"F2.wireOp",EDGE,"E16")])],"isStart":false}),"instanceName":"1"});
            var Q7;
            Q7=makeQuery(id+"F1.opExtrude","CAP_FACE",FACE,{"disambiguationData":[OSD([sQuery(id+"F0.wireOp",EDGE,"SqP7JoLz-BD9A-RXmz-Zu1V-RbqKSFD4Gl63"),sQuery(id+"F0.wireOp",EDGE,"Ud9Chbpr-zYe2-2spb-ifSY-rzAQWNdjOQxf"),sQuery(id+"F0.wireOp",EDGE,"bF6wv58Z-VzMq-CWjE-Sgwb-4WXWosELiao8"),sQuery(id+"F0.wireOp",EDGE,"cTkBJLnt-Smek-8MJw-4hbo-giizK2urv45t"),sQuery(id+"F0.wireOp",EDGE,"ae239fa6-1cef-4aa7-9151-0311c269b8940.MirrorCS"),sQuery(id+"F0.wireOp",EDGE,"ae239fa6-1cef-4aa7-9151-0311c269b8941.MirrorCS"),sQuery(id+"F0.wireOp",EDGE,"ae239fa6-1cef-4aa7-9151-0311c269b8943.MirrorCS"),sQuery(id+"F0.wireOp",EDGE,"ae239fa6-1cef-4aa7-9151-0311c269b8946.MirrorCS"),sQuery(id+"F0.wireOp",EDGE,"02da523c-332d-451a-b30c-e25d5381daab.1.0"),sQuery(id+"F0.wireOp",EDGE,"02da523c-332d-451a-b30c-e25d5381daab.1.1"),sQuery(id+"F0.wireOp",EDGE,"02da523c-332d-451a-b30c-e25d5381daab.1.2"),sQuery(id+"F0.wireOp",EDGE,"02da523c-332d-451a-b30c-e25d5381daab.1.5"),sQuery(id+"F0.wireOp",EDGE,"02da523c-332d-451a-b30c-e25d5381daab.1.6"),sQuery(id+"F0.wireOp",EDGE,"02da523c-332d-451a-b30c-e25d5381daab.1.8"),sQuery(id+"F0.wireOp",EDGE,"02da523c-332d-451a-b30c-e25d5381daab.1.9"),sQuery(id+"F0.wireOp",EDGE,"02da523c-332d-451a-b30c-e25d5381daab.1.15"),sQuery(id+"F0.wireOp",EDGE,"02da523c-332d-451a-b30c-e25d5381daab.1.16"),sQuery(id+"F0.wireOp",EDGE,"02da523c-332d-451a-b30c-e25d5381daab.2.0"),sQuery(id+"F0.wireOp",EDGE,"02da523c-332d-451a-b30c-e25d5381daab.2.1"),sQuery(id+"F0.wireOp",EDGE,"02da523c-332d-451a-b30c-e25d5381daab.2.2"),sQuery(id+"F0.wireOp",EDGE,"02da523c-332d-451a-b30c-e25d5381daab.2.5"),sQuery(id+"F0.wireOp",EDGE,"02da523c-332d-451a-b30c-e25d5381daab.2.6"),sQuery(id+"F0.wireOp",EDGE,"02da523c-332d-451a-b30c-e25d5381daab.2.8"),sQuery(id+"F0.wireOp",EDGE,"02da523c-332d-451a-b30c-e25d5381daab.2.9"),sQuery(id+"F0.wireOp",EDGE,"02da523c-332d-451a-b30c-e25d5381daab.2.11"),sQuery(id+"F0.wireOp",EDGE,"02da523c-332d-451a-b30c-e25d5381daab.2.15"),sQuery(id+"F0.wireOp",EDGE,"02da523c-332d-451a-b30c-e25d5381daab.2.16"),sQuery(id+"F0.wireOp",EDGE,"tuegAIGZ-9Pk6-ZTlW-QU7Y-IGKE2iZstJ9h"),sQuery(id+"F0.wireOp",EDGE,"fd02a02f-7cdf-416c-a631-e7393bf9c9300.MirrorC"),sQuery(id+"F0.wireOp",EDGE,"b5a6a487-fcb2-4526-9c33-14607ead2c7a.1.0"),sQuery(id+"F0.wireOp",EDGE,"b5a6a487-fcb2-4526-9c33-14607ead2c7a.1.1"),sQuery(id+"F0.wireOp",EDGE,"b5a6a487-fcb2-4526-9c33-14607ead2c7a.2.0"),sQuery(id+"F0.wireOp",EDGE,"b5a6a487-fcb2-4526-9c33-14607ead2c7a.2.1")])],"isStart":false});
            var Q8;
            Q8=makeQuery(id+"F1.opExtrude","CAP_FACE",FACE,{"disambiguationData":[OSD([sQuery(id+"F0.wireOp",EDGE,"4484d7a0-2c50-4ab7-845c-1fad09a73396"),sQuery(id+"F0.wireOp",EDGE,"vunMmcyM-OmEz-jSXp-RP42-2TM2nteFIjq3"),sQuery(id+"F0.wireOp",EDGE,"kAdxAM4n-0fVD-Q49A-3DVH-t19awp9mxCRN"),sQuery(id+"F0.wireOp",EDGE,"1fc718da-6f13-47b3-b5a0-f714b977743f0.MirrorCS"),sQuery(id+"F0.wireOp",EDGE,"0c3f0dc6-742d-4421-8c8e-992fc040e4260.MirrorCS"),sQuery(id+"F0.wireOp",EDGE,"NR2aZ9zS-O8kZ-dOxt-Ha0G-w07LVY2dGel9"),sQuery(id+"F0.wireOp",EDGE,"E0"),sQuery(id+"F0.wireOp",EDGE,"E1"),sQuery(id+"F0.wireOp",EDGE,"E2"),sQuery(id+"F0.wireOp",EDGE,"E3.MirrorCS"),sQuery(id+"F0.wireOp",EDGE,"E4.MirrorCS"),sQuery(id+"F0.wireOp",EDGE,"E5.MirrorCS"),sQuery(id+"F0.wireOp",EDGE,"b799197c-b9e2-4d90-802a-dec7aafa3731.1.0"),sQuery(id+"F0.wireOp",EDGE,"b799197c-b9e2-4d90-802a-dec7aafa3731.1.1"),sQuery(id+"F0.wireOp",EDGE,"b799197c-b9e2-4d90-802a-dec7aafa3731.1.2"),sQuery(id+"F0.wireOp",EDGE,"b799197c-b9e2-4d90-802a-dec7aafa3731.1.3"),sQuery(id+"F0.wireOp",EDGE,"b799197c-b9e2-4d90-802a-dec7aafa3731.1.4"),sQuery(id+"F0.wireOp",EDGE,"b799197c-b9e2-4d90-802a-dec7aafa3731.1.5"),sQuery(id+"F0.wireOp",EDGE,"b799197c-b9e2-4d90-802a-dec7aafa3731.2.0"),sQuery(id+"F0.wireOp",EDGE,"b799197c-b9e2-4d90-802a-dec7aafa3731.2.1"),sQuery(id+"F0.wireOp",EDGE,"b799197c-b9e2-4d90-802a-dec7aafa3731.2.2"),sQuery(id+"F0.wireOp",EDGE,"b799197c-b9e2-4d90-802a-dec7aafa3731.2.3"),sQuery(id+"F0.wireOp",EDGE,"b799197c-b9e2-4d90-802a-dec7aafa3731.2.4"),sQuery(id+"F0.wireOp",EDGE,"b799197c-b9e2-4d90-802a-dec7aafa3731.2.5"),sQuery(id+"F0.wireOp",EDGE,"Wg4TRRuH-37hh-Xavb-2tcF-YoE0x18wPgdB"),sQuery(id+"F0.wireOp",EDGE,"0f9c7b85-d36a-485b-916f-4e3243d4aea60.MirrorCS"),sQuery(id+"F0.wireOp",EDGE,"b2d11125-5d0d-4662-a4de-013f4188032f.1.0"),sQuery(id+"F0.wireOp",EDGE,"b2d11125-5d0d-4662-a4de-013f4188032f.1.2"),sQuery(id+"F0.wireOp",EDGE,"b2d11125-5d0d-4662-a4de-013f4188032f.1.3"),sQuery(id+"F0.wireOp",EDGE,"b2d11125-5d0d-4662-a4de-013f4188032f.1.7"),sQuery(id+"F0.wireOp",EDGE,"b2d11125-5d0d-4662-a4de-013f4188032f.1.8"),sQuery(id+"F0.wireOp",EDGE,"b2d11125-5d0d-4662-a4de-013f4188032f.1.9"),sQuery(id+"F0.wireOp",EDGE,"b2d11125-5d0d-4662-a4de-013f4188032f.1.10"),sQuery(id+"F0.wireOp",EDGE,"b2d11125-5d0d-4662-a4de-013f4188032f.2.0"),sQuery(id+"F0.wireOp",EDGE,"b2d11125-5d0d-4662-a4de-013f4188032f.2.2"),sQuery(id+"F0.wireOp",EDGE,"b2d11125-5d0d-4662-a4de-013f4188032f.2.3"),sQuery(id+"F0.wireOp",EDGE,"b2d11125-5d0d-4662-a4de-013f4188032f.2.7"),sQuery(id+"F0.wireOp",EDGE,"b2d11125-5d0d-4662-a4de-013f4188032f.2.8"),sQuery(id+"F0.wireOp",EDGE,"b2d11125-5d0d-4662-a4de-013f4188032f.2.9"),sQuery(id+"F0.wireOp",EDGE,"b2d11125-5d0d-4662-a4de-013f4188032f.2.10")])],"isStart":false});
            chamfer(context, id + "F15", {"entities" : qUnion([Q0, Q1, Q2, Q3, Q4, Q5, Q6, Q7, Q8]), "width" : .4 * mm, "tangentPropagation" : true});
        }
    });
